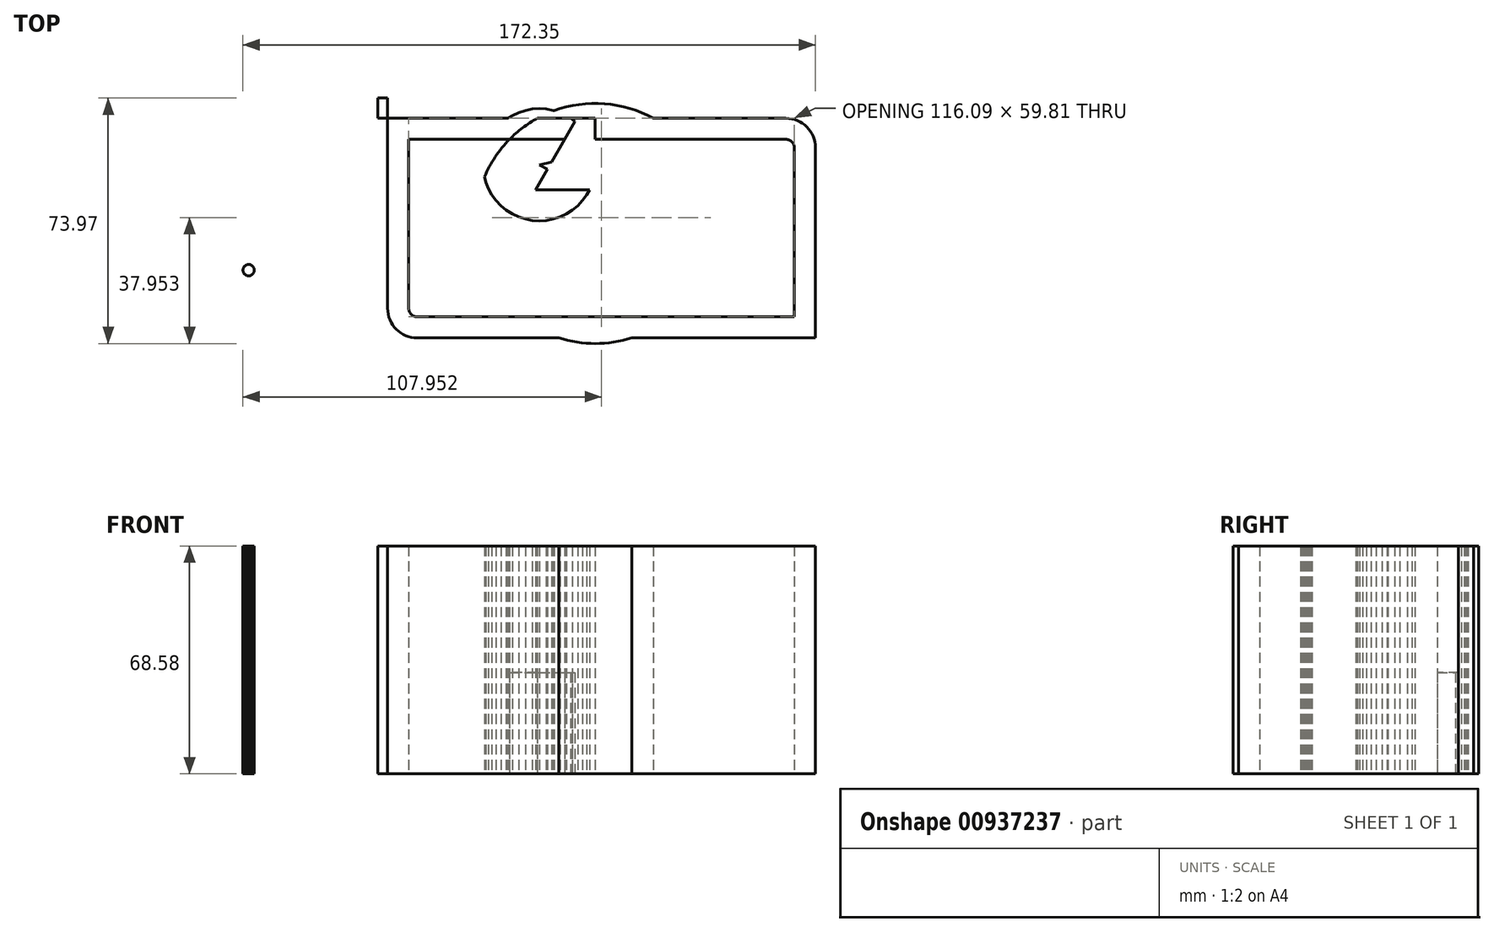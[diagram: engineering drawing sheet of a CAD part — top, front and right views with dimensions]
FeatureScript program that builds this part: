
annotation { "Feature Type Name" : "Feature", "Feature Type Description" : "" }
export const myFeature = defineFeature(function(context is Context, id is Id, definition is map)
    precondition{}
    {
        {
            var Q0;
            Q0=qCreatedBy(makeId("Top.planeOp"),FACE);
            var sketch = newSketch(context, id + "F0", { "sketchPlane" : qUnion([Q0])});
            skCircle(sketch, "E0", {"center": v(0, 0) * mm, "radius": 36.17 * mm});
            skLineSegment(sketch, "E1.bottom", {"start": v(-65.45, 31.69) * mm, "end": v(-62.52, 31.69) * mm});
            skLineSegment(sketch, "E1.top", {"start": v(-65.45, 37.8) * mm, "end": v(-62.52, 37.8) * mm});
            skLineSegment(sketch, "E1.left", {"start": v(-65.45, 31.69) * mm, "end": v(-65.45, 37.8) * mm});
            skLineSegment(sketch, "E1.right", {"start": v(-62.52, 31.69) * mm, "end": v(-62.52, 37.8) * mm});
            skLineSegment(sketch, "E2.bottom", {"start": v(-62.52, 31.69) * mm, "end": v(0, 31.69) * mm});
            skLineSegment(sketch, "E2.top", {"start": v(-62.52, 0) * mm, "end": v(0, 0) * mm});
            skLineSegment(sketch, "E2.left", {"start": v(-62.52, 31.69) * mm, "end": v(-62.52, 0) * mm});
            skLineSegment(sketch, "E2.right", {"start": v(0, 31.69) * mm, "end": v(0, 0) * mm});
            skLineSegment(sketch, "E3.bottom", {"start": v(-53.63, -34.47) * mm, "end": v(0, -34.47) * mm});
            skLineSegment(sketch, "E3.left", {"start": v(-62.52, -25.58) * mm, "end": v(-62.52, 0) * mm});
            skLineSegment(sketch, "E3.right", {"start": v(0, -34.47) * mm, "end": v(0, 0) * mm});
            skLineSegment(sketch, "E4.bottom", {"start": v(-65.45, 34.74) * mm, "end": v(-62.52, 34.74) * mm});
            skLineSegment(sketch, "E4.top", {"start": v(-65.45, 34.74) * mm, "end": v(-62.52, 34.74) * mm});
            skLineSegment(sketch, "E4.left", {"start": v(-65.45, 34.74) * mm, "end": v(-65.45, 34.74) * mm});
            skLineSegment(sketch, "E4.right", {"start": v(-62.52, 34.74) * mm, "end": v(-62.52, 34.74) * mm});
            skLineSegment(sketch, "E5.bottom", {"start": v(0, 31.69) * mm, "end": v(57.39, 31.69) * mm});
            skLineSegment(sketch, "E5.top", {"start": v(0, 0) * mm, "end": v(66.28, 0) * mm});
            skLineSegment(sketch, "E5.right", {"start": v(66.28, 22.8) * mm, "end": v(66.28, 0) * mm});
            skLineSegment(sketch, "E6.bottom", {"start": v(66.28, 0) * mm, "end": v(0, 0) * mm});
            skLineSegment(sketch, "E6.top", {"start": v(66.28, -34.47) * mm, "end": v(0, -34.47) * mm});
            skLineSegment(sketch, "E6.left", {"start": v(66.28, 0) * mm, "end": v(66.28, -34.47) * mm});
            skLineSegment(sketch, "E6.right", {"start": v(0, 0) * mm, "end": v(0, -34.47) * mm});
            skCircle(sketch, "E7.cCircle", {"center": v(-5.72, 17.25) * mm, "radius": 7.1 * mm, "construction": true});
            skLineSegment(sketch, "E7.0", {"start": v(6.57, 10.15) * mm, "end": v(-18.01, 10.15) * mm});
            skLineSegment(sketch, "E7.1", {"start": v(-18.01, 10.15) * mm, "end": v(-5.72, 31.44) * mm});
            skLineSegment(sketch, "E7.2", {"start": v(-5.72, 31.44) * mm, "end": v(6.57, 10.15) * mm});
            skPoint(sketch, "E7.0.midPoint", {"position": v(-5.72, 10.15) * mm});
            skCircle(sketch, "E8.cCircle", {"center": v(-18.01, 10.15) * mm, "radius": 7.1 * mm, "construction": true});
            skLineSegment(sketch, "E8.0", {"start": v(-12.06, 14.91) * mm, "end": v(-16.87, 17.69) * mm});
            skLineSegment(sketch, "E8.1", {"start": v(-12.06, 14.91) * mm, "end": v(-13.18, 18.52) * mm});
            skLineSegment(sketch, "E8.2", {"start": v(-13.18, 18.52) * mm, "end": v(-16.87, 17.69) * mm});
            skPoint(sketch, "E8.0.midPoint", {"position": v(-14.47, 16.3) * mm});
            skCircle(sketch, "E9.cCircle", {"center": v(-16.87, 17.69) * mm, "radius": 16.87 * mm, "construction": true});
            skLineSegment(sketch, "E9.0", {"start": v(0, 18.75) * mm, "end": v(0, 16.63) * mm});
            skLineSegment(sketch, "E9.1", {"start": v(0, 16.63) * mm, "end": v(-0.27, 14.52) * mm});
            skLineSegment(sketch, "E9.2", {"start": v(-0.27, 14.52) * mm, "end": v(-0.8, 12.46) * mm});
            skLineSegment(sketch, "E9.3", {"start": v(-0.8, 12.46) * mm, "end": v(-1.58, 10.49) * mm});
            skLineSegment(sketch, "E9.4", {"start": v(-1.58, 10.49) * mm, "end": v(-2.6, 8.63) * mm});
            skLineSegment(sketch, "E9.5", {"start": v(-2.6, 8.63) * mm, "end": v(-3.85, 6.91) * mm});
            skLineSegment(sketch, "E9.6", {"start": v(-3.85, 6.91) * mm, "end": v(-5.3, 5.36) * mm});
            skLineSegment(sketch, "E9.7", {"start": v(-5.3, 5.36) * mm, "end": v(-6.93, 4.01) * mm});
            skLineSegment(sketch, "E9.8", {"start": v(-6.93, 4.01) * mm, "end": v(-8.73, 2.87) * mm});
            skLineSegment(sketch, "E9.9", {"start": v(-8.73, 2.87) * mm, "end": v(-10.65, 1.97) * mm});
            skLineSegment(sketch, "E9.10", {"start": v(-10.65, 1.97) * mm, "end": v(-12.67, 1.31) * mm});
            skLineSegment(sketch, "E9.11", {"start": v(-12.67, 1.31) * mm, "end": v(-14.75, 0.92) * mm});
            skLineSegment(sketch, "E9.12", {"start": v(-14.75, 0.92) * mm, "end": v(-16.87, 0.78) * mm});
            skLineSegment(sketch, "E9.13", {"start": v(-16.87, 0.78) * mm, "end": v(-18.99, 0.92) * mm});
            skLineSegment(sketch, "E9.14", {"start": v(-18.99, 0.92) * mm, "end": v(-21.07, 1.31) * mm});
            skLineSegment(sketch, "E9.15", {"start": v(-21.07, 1.31) * mm, "end": v(-23.1, 1.97) * mm});
            skLineSegment(sketch, "E9.16", {"start": v(-23.1, 1.97) * mm, "end": v(-25.01, 2.87) * mm});
            skLineSegment(sketch, "E9.17", {"start": v(-25.01, 2.87) * mm, "end": v(-26.8, 4.01) * mm});
            skLineSegment(sketch, "E9.18", {"start": v(-26.8, 4.01) * mm, "end": v(-28.44, 5.36) * mm});
            skLineSegment(sketch, "E9.19", {"start": v(-28.44, 5.36) * mm, "end": v(-29.9, 6.91) * mm});
            skLineSegment(sketch, "E9.20", {"start": v(-29.9, 6.91) * mm, "end": v(-31.14, 8.63) * mm});
            skLineSegment(sketch, "E9.21", {"start": v(-31.14, 8.63) * mm, "end": v(-32.17, 10.49) * mm});
            skLineSegment(sketch, "E9.22", {"start": v(-32.17, 10.49) * mm, "end": v(-32.95, 12.46) * mm});
            skLineSegment(sketch, "E9.23", {"start": v(-32.95, 12.46) * mm, "end": v(-33.48, 14.52) * mm});
            skLineSegment(sketch, "E9.24", {"start": v(-33.48, 14.52) * mm, "end": v(-33.74, 16.63) * mm});
            skLineSegment(sketch, "E9.25", {"start": v(-33.74, 16.63) * mm, "end": v(-33.74, 18.75) * mm});
            skLineSegment(sketch, "E9.26", {"start": v(-33.74, 18.75) * mm, "end": v(-33.48, 20.85) * mm});
            skLineSegment(sketch, "E9.27", {"start": v(-33.48, 20.85) * mm, "end": v(-32.95, 22.91) * mm});
            skLineSegment(sketch, "E9.28", {"start": v(-32.95, 22.91) * mm, "end": v(-32.17, 24.88) * mm});
            skLineSegment(sketch, "E9.29", {"start": v(-32.17, 24.88) * mm, "end": v(-31.14, 26.74) * mm});
            skLineSegment(sketch, "E9.30", {"start": v(-31.14, 26.74) * mm, "end": v(-29.9, 28.46) * mm});
            skLineSegment(sketch, "E9.31", {"start": v(-29.9, 28.46) * mm, "end": v(-28.44, 30) * mm});
            skLineSegment(sketch, "E9.32", {"start": v(-28.44, 30) * mm, "end": v(-26.8, 31.36) * mm});
            skLineSegment(sketch, "E9.33", {"start": v(-26.8, 31.36) * mm, "end": v(-25.01, 32.5) * mm});
            skLineSegment(sketch, "E9.34", {"start": v(-25.01, 32.5) * mm, "end": v(-23.1, 33.4) * mm});
            skLineSegment(sketch, "E9.35", {"start": v(-23.1, 33.4) * mm, "end": v(-21.07, 34.06) * mm});
            skLineSegment(sketch, "E9.36", {"start": v(-21.07, 34.06) * mm, "end": v(-18.99, 34.46) * mm});
            skLineSegment(sketch, "E9.37", {"start": v(-18.99, 34.46) * mm, "end": v(-16.87, 34.6) * mm});
            skLineSegment(sketch, "E9.38", {"start": v(-16.87, 34.6) * mm, "end": v(-14.75, 34.46) * mm});
            skLineSegment(sketch, "E9.39", {"start": v(-14.75, 34.46) * mm, "end": v(-12.67, 34.06) * mm});
            skLineSegment(sketch, "E9.40", {"start": v(-12.67, 34.06) * mm, "end": v(-10.65, 33.4) * mm});
            skLineSegment(sketch, "E9.41", {"start": v(-10.65, 33.4) * mm, "end": v(-8.73, 32.5) * mm});
            skLineSegment(sketch, "E9.42", {"start": v(-8.73, 32.5) * mm, "end": v(-6.93, 31.36) * mm});
            skLineSegment(sketch, "E9.43", {"start": v(-6.93, 31.36) * mm, "end": v(-5.3, 30) * mm});
            skLineSegment(sketch, "E9.44", {"start": v(-5.3, 30) * mm, "end": v(-3.85, 28.46) * mm});
            skLineSegment(sketch, "E9.45", {"start": v(-3.85, 28.46) * mm, "end": v(-2.6, 26.74) * mm});
            skLineSegment(sketch, "E9.46", {"start": v(-2.6, 26.74) * mm, "end": v(-1.58, 24.88) * mm});
            skLineSegment(sketch, "E9.47", {"start": v(-1.58, 24.88) * mm, "end": v(-0.8, 22.91) * mm});
            skLineSegment(sketch, "E9.48", {"start": v(-0.8, 22.91) * mm, "end": v(-0.27, 20.85) * mm});
            skLineSegment(sketch, "E9.49", {"start": v(-0.27, 20.85) * mm, "end": v(0, 18.75) * mm});
            skPoint(sketch, "E9.0.midPoint", {"position": v(0, 17.69) * mm});
            skCircle(sketch, "E10.cCircle", {"center": v(-104.36, -14.07) * mm, "radius": 1.71 * mm, "construction": true});
            skLineSegment(sketch, "E10.0", {"start": v(-102.64, -13.96) * mm, "end": v(-102.64, -14.18) * mm});
            skLineSegment(sketch, "E10.1", {"start": v(-102.64, -14.18) * mm, "end": v(-102.67, -14.4) * mm});
            skLineSegment(sketch, "E10.2", {"start": v(-102.67, -14.4) * mm, "end": v(-102.72, -14.6) * mm});
            skLineSegment(sketch, "E10.3", {"start": v(-102.72, -14.6) * mm, "end": v(-102.8, -14.8) * mm});
            skLineSegment(sketch, "E10.4", {"start": v(-102.8, -14.8) * mm, "end": v(-102.9, -14.99) * mm});
            skLineSegment(sketch, "E10.5", {"start": v(-102.9, -14.99) * mm, "end": v(-103.03, -15.16) * mm});
            skLineSegment(sketch, "E10.6", {"start": v(-103.03, -15.16) * mm, "end": v(-103.18, -15.32) * mm});
            skLineSegment(sketch, "E10.7", {"start": v(-103.18, -15.32) * mm, "end": v(-103.35, -15.46) * mm});
            skLineSegment(sketch, "E10.8", {"start": v(-103.35, -15.46) * mm, "end": v(-103.53, -15.57) * mm});
            skLineSegment(sketch, "E10.9", {"start": v(-103.53, -15.57) * mm, "end": v(-103.72, -15.66) * mm});
            skLineSegment(sketch, "E10.10", {"start": v(-103.72, -15.66) * mm, "end": v(-103.93, -15.73) * mm});
            skLineSegment(sketch, "E10.11", {"start": v(-103.93, -15.73) * mm, "end": v(-104.14, -15.77) * mm});
            skLineSegment(sketch, "E10.12", {"start": v(-104.14, -15.77) * mm, "end": v(-104.36, -15.79) * mm});
            skLineSegment(sketch, "E10.13", {"start": v(-104.36, -15.79) * mm, "end": v(-104.57, -15.77) * mm});
            skLineSegment(sketch, "E10.14", {"start": v(-104.57, -15.77) * mm, "end": v(-104.78, -15.73) * mm});
            skLineSegment(sketch, "E10.15", {"start": v(-104.78, -15.73) * mm, "end": v(-104.99, -15.66) * mm});
            skLineSegment(sketch, "E10.16", {"start": v(-104.99, -15.66) * mm, "end": v(-105.18, -15.57) * mm});
            skLineSegment(sketch, "E10.17", {"start": v(-105.18, -15.57) * mm, "end": v(-105.36, -15.46) * mm});
            skLineSegment(sketch, "E10.18", {"start": v(-105.36, -15.46) * mm, "end": v(-105.53, -15.32) * mm});
            skLineSegment(sketch, "E10.19", {"start": v(-105.53, -15.32) * mm, "end": v(-105.68, -15.16) * mm});
            skLineSegment(sketch, "E10.20", {"start": v(-105.68, -15.16) * mm, "end": v(-105.8, -14.99) * mm});
            skLineSegment(sketch, "E10.21", {"start": v(-105.8, -14.99) * mm, "end": v(-105.9, -14.8) * mm});
            skLineSegment(sketch, "E10.22", {"start": v(-105.9, -14.8) * mm, "end": v(-105.99, -14.6) * mm});
            skLineSegment(sketch, "E10.23", {"start": v(-105.99, -14.6) * mm, "end": v(-106.04, -14.4) * mm});
            skLineSegment(sketch, "E10.24", {"start": v(-106.04, -14.4) * mm, "end": v(-106.07, -14.18) * mm});
            skLineSegment(sketch, "E10.25", {"start": v(-106.07, -14.18) * mm, "end": v(-106.07, -13.96) * mm});
            skLineSegment(sketch, "E10.26", {"start": v(-106.07, -13.96) * mm, "end": v(-106.04, -13.75) * mm});
            skLineSegment(sketch, "E10.27", {"start": v(-106.04, -13.75) * mm, "end": v(-105.99, -13.54) * mm});
            skLineSegment(sketch, "E10.28", {"start": v(-105.99, -13.54) * mm, "end": v(-105.9, -13.34) * mm});
            skLineSegment(sketch, "E10.29", {"start": v(-105.9, -13.34) * mm, "end": v(-105.8, -13.15) * mm});
            skLineSegment(sketch, "E10.30", {"start": v(-105.8, -13.15) * mm, "end": v(-105.68, -12.98) * mm});
            skLineSegment(sketch, "E10.31", {"start": v(-105.68, -12.98) * mm, "end": v(-105.53, -12.82) * mm});
            skLineSegment(sketch, "E10.32", {"start": v(-105.53, -12.82) * mm, "end": v(-105.36, -12.68) * mm});
            skLineSegment(sketch, "E10.33", {"start": v(-105.36, -12.68) * mm, "end": v(-105.18, -12.57) * mm});
            skLineSegment(sketch, "E10.34", {"start": v(-105.18, -12.57) * mm, "end": v(-104.99, -12.47) * mm});
            skLineSegment(sketch, "E10.35", {"start": v(-104.99, -12.47) * mm, "end": v(-104.78, -12.4) * mm});
            skLineSegment(sketch, "E10.36", {"start": v(-104.78, -12.4) * mm, "end": v(-104.57, -12.37) * mm});
            skLineSegment(sketch, "E10.37", {"start": v(-104.57, -12.37) * mm, "end": v(-104.36, -12.35) * mm});
            skLineSegment(sketch, "E10.38", {"start": v(-104.36, -12.35) * mm, "end": v(-104.14, -12.37) * mm});
            skLineSegment(sketch, "E10.39", {"start": v(-104.14, -12.37) * mm, "end": v(-103.93, -12.4) * mm});
            skLineSegment(sketch, "E10.40", {"start": v(-103.93, -12.4) * mm, "end": v(-103.72, -12.47) * mm});
            skLineSegment(sketch, "E10.41", {"start": v(-103.72, -12.47) * mm, "end": v(-103.53, -12.57) * mm});
            skLineSegment(sketch, "E10.42", {"start": v(-103.53, -12.57) * mm, "end": v(-103.35, -12.68) * mm});
            skLineSegment(sketch, "E10.43", {"start": v(-103.35, -12.68) * mm, "end": v(-103.18, -12.82) * mm});
            skLineSegment(sketch, "E10.44", {"start": v(-103.18, -12.82) * mm, "end": v(-103.03, -12.98) * mm});
            skLineSegment(sketch, "E10.45", {"start": v(-103.03, -12.98) * mm, "end": v(-102.9, -13.15) * mm});
            skLineSegment(sketch, "E10.46", {"start": v(-102.9, -13.15) * mm, "end": v(-102.8, -13.34) * mm});
            skLineSegment(sketch, "E10.47", {"start": v(-102.8, -13.34) * mm, "end": v(-102.72, -13.54) * mm});
            skLineSegment(sketch, "E10.48", {"start": v(-102.72, -13.54) * mm, "end": v(-102.67, -13.75) * mm});
            skLineSegment(sketch, "E10.49", {"start": v(-102.67, -13.75) * mm, "end": v(-102.64, -13.96) * mm});
            skPoint(sketch, "E10.0.midPoint", {"position": v(-102.64, -14.07) * mm});
            skPoint(sketch, "E11.visualSharp", {"position": v(-62.52, -34.47) * mm});
            skArc(sketch, "E11.filletArc", {"start": v(-62.52, -25.58) * mm, "mid": v(-59.91, -31.87) * mm, "end": v(-53.63, -34.47) * mm});
            skPoint(sketch, "E12.visualSharp", {"position": v(66.28, 31.69) * mm});
            skArc(sketch, "E12.filletArc", {"start": v(66.28, 22.8) * mm, "mid": v(63.68, 29.08) * mm, "end": v(57.39, 31.69) * mm});
            skLineSegment(sketch, "E13.0", {"start": v(-62.52, 38.04) * mm, "end": v(0, 38.04) * mm});
            skLineSegment(sketch, "E14.0", {"start": v(-56.17, 25.34) * mm, "end": v(-56.17, 0) * mm});
            skLineSegment(sketch, "E14.1", {"start": v(-56.17, -25.58) * mm, "end": v(-56.17, 0) * mm});
            skLineSegment(sketch, "E14.2", {"start": v(-56.17, 25.34) * mm, "end": v(0, 25.34) * mm});
            skArc(sketch, "E14.3", {"start": v(-56.17, -25.58) * mm, "mid": v(-55.42, -27.38) * mm, "end": v(-53.63, -28.12) * mm});
            skLineSegment(sketch, "E14.4", {"start": v(-53.63, -28.12) * mm, "end": v(0, -28.12) * mm});
            skLineSegment(sketch, "E14.5", {"start": v(59.93, -28.12) * mm, "end": v(0, -28.12) * mm});
            skLineSegment(sketch, "E14.6", {"start": v(0, 25.34) * mm, "end": v(57.39, 25.34) * mm});
            skArc(sketch, "E14.7", {"start": v(59.93, 22.8) * mm, "mid": v(59.18, 24.6) * mm, "end": v(57.39, 25.34) * mm});
            skLineSegment(sketch, "E14.8", {"start": v(59.93, 22.8) * mm, "end": v(59.93, 0) * mm});
            skLineSegment(sketch, "E14.9", {"start": v(59.93, 0) * mm, "end": v(59.93, -28.12) * mm});
            skLineSegment(sketch, "E15.1.0.0", {"start": v(-40.05, 34.74) * mm, "end": v(-37.12, 34.74) * mm});
            skLineSegment(sketch, "E15.2.0.0", {"start": v(-14.65, 34.74) * mm, "end": v(-11.72, 34.74) * mm});
            skLineSegment(sketch, "E15.direction1", {"start": v(-65.45, 34.74) * mm, "end": v(-40.05, 34.74) * mm, "construction": true});
            skSolve(sketch);
        }
        {
            var Q0;
            {var subQ4=sQuery(id+"F0.wireOp",EDGE,"E2.left");Q0=makeQuery(id+"F0.imprint","IMPRINT",FACE,{"disambiguationData":[TD([[makeQuery(id+"F0.imprint","IMPRINT",EDGE,{"derivedFrom":subQ4}),1.0]])]});}
            extrude(context, id + "F1", {"entities" : qUnion([Q0]), "depth" : 25.4 * mm, "offsetDistance" : 25.4 * mm});
        }
        {
            var Q0;
            Q0 = qSketchRegion(id + "F0", true);
            extrude(context, id + "F2", {"entities" : qUnion([Q0]), "operationType" : NewBodyOperationType.ADD, "depth" : 25.4 * mm, "offsetDistance" : 25.4 * mm});
        }
        {
            var Q0;
            Q0 = qSketchRegion(id + "F0", true);
            var Q1;
            {var subQ0=sQuery(id+"F0.wireOp",EDGE,"E8.2");Q1=makeQuery(id+"F0.imprint","IMPRINT",FACE,{"disambiguationData":[TD([[makeQuery(id+"F0.imprint","IMPRINT",EDGE,{"derivedFrom":subQ0}),-1.0]])]});}
            extrude(context, id + "F3", {"entities" : qUnion([Q0, Q1]), "operationType" : NewBodyOperationType.ADD, "depth" : 68.58 * mm, "offsetDistance" : 25.4 * mm});
        }
        {
            var Q0;
            {var subQ3=sQuery(id+"F0.wireOp",EDGE,"E2.bottom");var subQ9=sQuery(id+"F0.wireOp",EDGE,"E0");var subQ10=makeQuery(id+"F0.imprint","INTERSECT",VERTEX,{"derivedFrom":[subQ9,subQ3]});Q0=makeQuery(id+"F0.imprint","IMPRINT",FACE,{"disambiguationData":[TD([[makeQuery(id+"F0.imprint","IMPRINT",EDGE,{"disambiguationData":[TD([[subQ10,-1.0]])],"derivedFrom":subQ9}),1.0]])]});}
            extrude(context, id + "F4", {"entities" : qUnion([Q0]), "depth" : 30.48 * mm, "offsetDistance" : 25.4 * mm});
        }
        {
            var Q0;
            Q0=sQuery(id+"F0.wireOp",EDGE,"E7.0");
            var Q1;
            Q1=sQuery(id+"F0.wireOp",EDGE,"E7.1");
            var Q2;
            Q2=sQuery(id+"F0.wireOp",EDGE,"E7.2");
            extrude(context, id + "F5", {"bodyType" : ToolBodyType.SURFACE, "surfaceEntities" : qUnion([Q0, Q1, Q2]), "depth" : 73.66 * mm, "offsetDistance" : 25.4 * mm});
        }
    });
